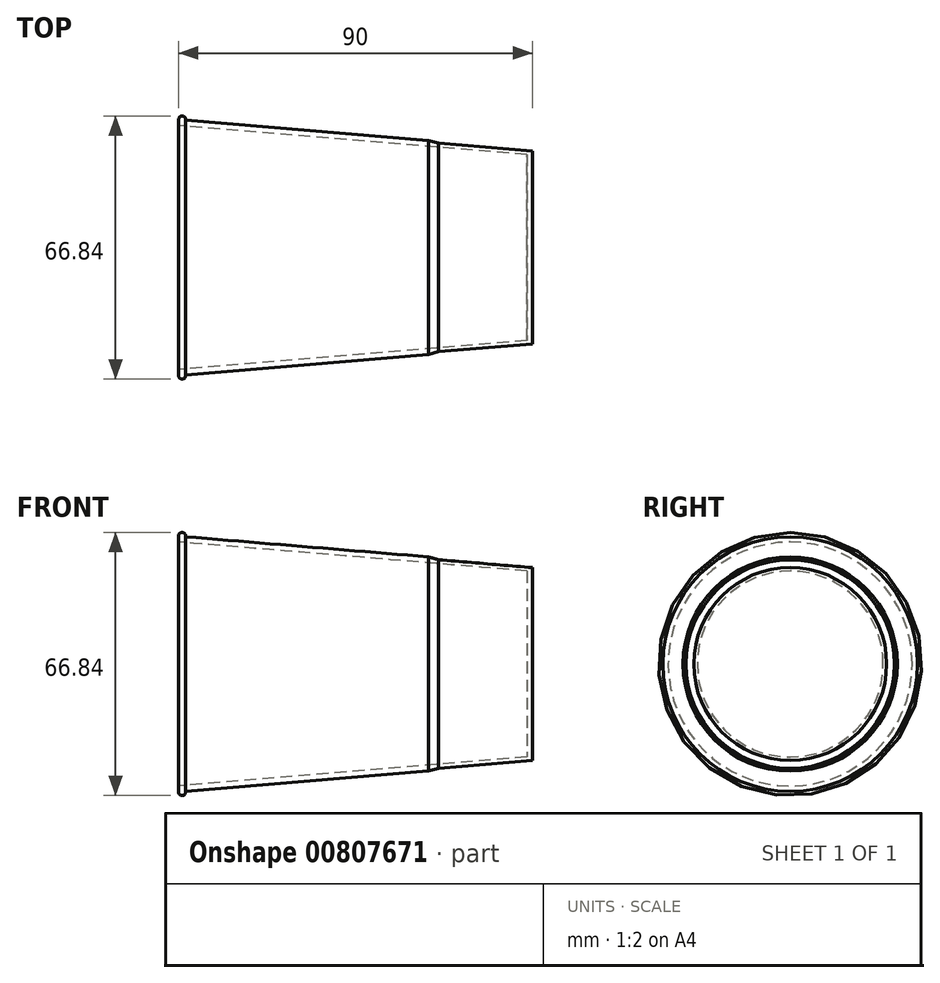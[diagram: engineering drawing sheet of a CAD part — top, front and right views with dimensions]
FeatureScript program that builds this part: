
annotation { "Feature Type Name" : "Feature", "Feature Type Description" : "" }
export const myFeature = defineFeature(function(context is Context, id is Id, definition is map)
    precondition{}
    {
        {
            var Q0;
            Q0=qCreatedBy(makeId("Front.planeOp"),FACE);
            var sketch = newSketch(context, id + "F0", { "sketchPlane" : qUnion([Q0])});
            skLineSegment(sketch, "E0", {"start": v(-129, 0) * mm, "end": v(127.52, 0) * mm, "construction": true});
            skLineSegment(sketch, "E1", {"start": v(0, 31) * mm, "end": v(0, 32.5) * mm});
            skLineSegment(sketch, "E2", {"start": v(90, 0) * mm, "end": v(90, 24.5) * mm});
            skLineSegment(sketch, "E3", {"start": v(1.84, 32.35) * mm, "end": v(63.55, 27.2) * mm});
            skLineSegment(sketch, "E4.0", {"start": v(88.5, 0) * mm, "end": v(88.5, 23.62) * mm});
            skLineSegment(sketch, "E4.1", {"start": v(0, 31) * mm, "end": v(88.5, 23.62) * mm});
            skLineSegment(sketch, "E5", {"start": v(88.5, 0) * mm, "end": v(90, 0) * mm});
            skArc(sketch, "E6", {"start": v(1.84, 32.35) * mm, "mid": v(1, 33.42) * mm, "end": v(0, 32.5) * mm});
            skLineSegment(sketch, "E7.0", {"start": v(66.09, 26.5) * mm, "end": v(89.96, 24.5) * mm});
            skLineSegment(sketch, "E8", {"start": v(66.09, 26.5) * mm, "end": v(63.55, 27.2) * mm});
            skLineSegment(sketch, "E9", {"start": v(89.96, 24.5) * mm, "end": v(90, 24.5) * mm});
            skPoint(sketch, "E10.orphan", {"position": v(90, 25) * mm});
            skSolve(sketch);
        }
        {
            var Q0;
            Q0 = qSketchRegion(id + "F0", true);
            var Q1;
            Q1=sQuery(id+"F0.wireOp",EDGE,"E0");
            revolve(context, id + "F1", {"surfaceOperationType" : NewSurfaceOperationType.NEW, "entities" : qUnion([Q0]), "axis" : qUnion([Q1]), "revolveType" : RevolveType.FULL});
        }
    });
